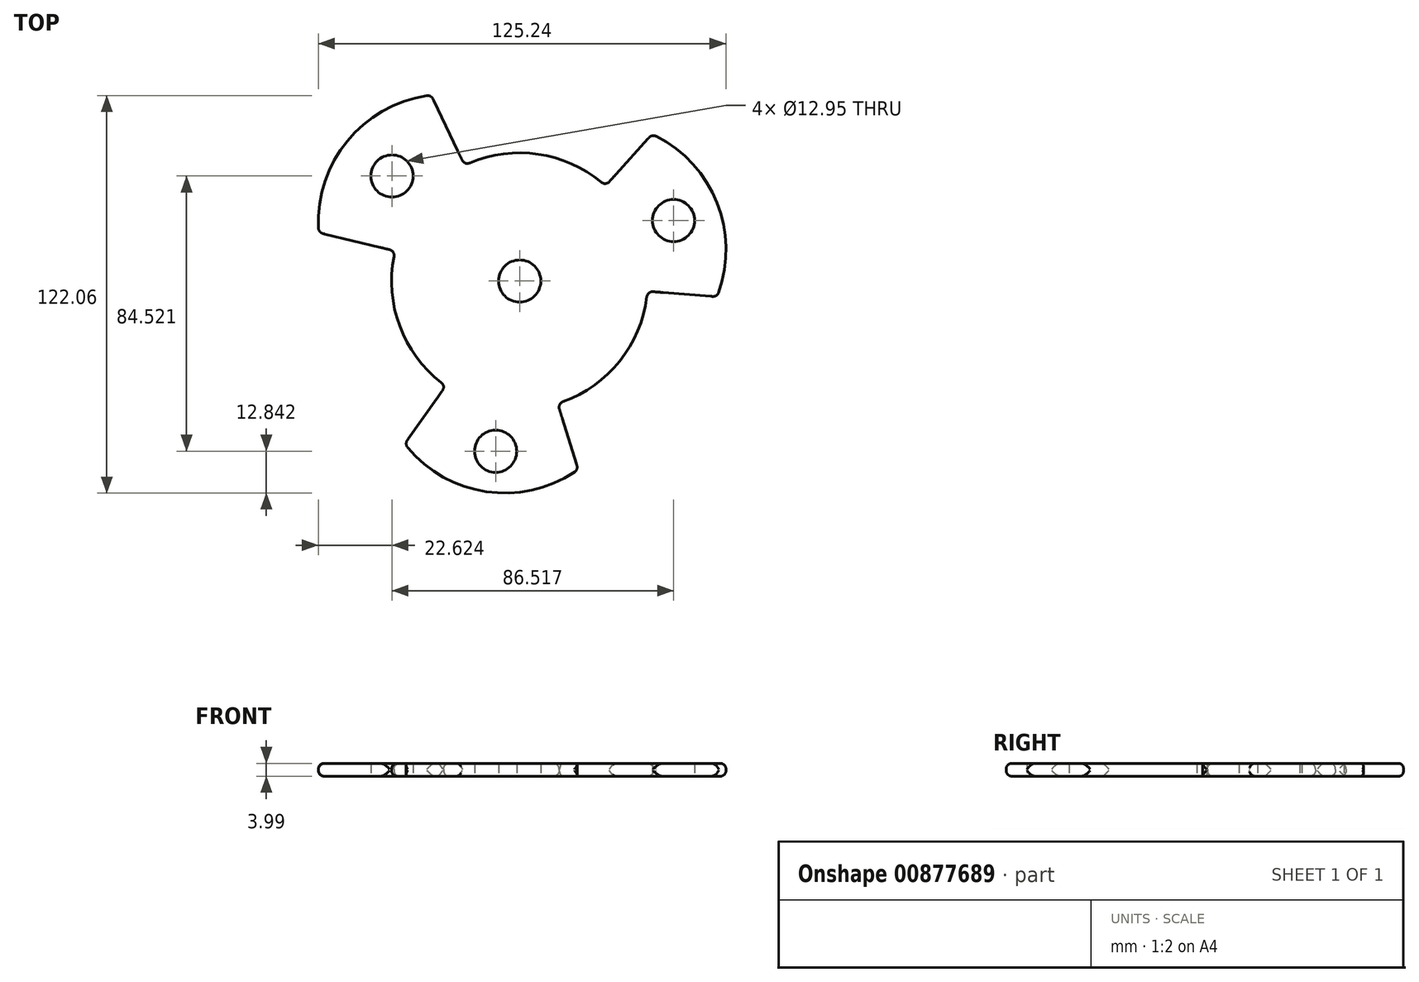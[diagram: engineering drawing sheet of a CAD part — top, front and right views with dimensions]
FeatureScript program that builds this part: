
annotation { "Feature Type Name" : "Feature", "Feature Type Description" : "" }
export const myFeature = defineFeature(function(context is Context, id is Id, definition is map)
    precondition{}
    {
        {
            var Q0;
            Q0=qCreatedBy(makeId("Top.planeOp"),FACE);
            var sketch = newSketch(context, id + "F0", { "sketchPlane" : qUnion([Q0])});
            skCircle(sketch, "E0", {"center": v(-46.46, 55.46) * mm, "radius": 6.48 * mm});
            skCircle(sketch, "E1", {"center": v(40.06, 41.79) * mm, "radius": 6.48 * mm});
            skCircle(sketch, "E2", {"center": v(-14.6, -29.06) * mm, "radius": 6.48 * mm});
            skCircle(sketch, "E3", {"center": v(-7.22, 23.2) * mm, "radius": 6.48 * mm});
            skCircle(sketch, "E4", {"center": v(-7.22, 23.2) * mm, "radius": 39.37 * mm});
            skCircle(sketch, "E5", {"center": v(-7.22, 23.2) * mm, "radius": 35.56 * mm});
            skLineSegment(sketch, "E6", {"start": v(-7.22, 23.2) * mm, "end": v(-68.95, 38.1) * mm});
            skLineSegment(sketch, "E7", {"start": v(-68.95, 38.1) * mm, "end": v(-7.22, 23.2) * mm});
            skLineSegment(sketch, "E8", {"start": v(-7.22, 23.2) * mm, "end": v(-42.53, -26.81) * mm});
            skLineSegment(sketch, "E9", {"start": v(-42.53, -26.81) * mm, "end": v(-7.22, 23.2) * mm});
            skLineSegment(sketch, "E10", {"start": v(-7.22, 23.2) * mm, "end": v(-34.4, 80.31) * mm});
            skLineSegment(sketch, "E11", {"start": v(-34.4, 80.31) * mm, "end": v(-7.22, 23.2) * mm});
            skLineSegment(sketch, "E12", {"start": v(-7.22, 23.2) * mm, "end": v(33.44, 68.27) * mm});
            skLineSegment(sketch, "E13", {"start": v(33.44, 68.27) * mm, "end": v(-7.22, 23.2) * mm});
            skLineSegment(sketch, "E14", {"start": v(53.4, 18.36) * mm, "end": v(-7.22, 23.2) * mm});
            skLineSegment(sketch, "E15", {"start": v(-7.22, 23.2) * mm, "end": v(10.74, -34.68) * mm});
            skArc(sketch, "E16", {"start": v(-34.4, 80.31) * mm, "mid": v(-60.2, 66.18) * mm, "end": v(-68.95, 38.1) * mm});
            skArc(sketch, "E17", {"start": v(53.4, 18.36) * mm, "mid": v(53.37, 47.3) * mm, "end": v(33.44, 68.27) * mm});
            skArc(sketch, "E18", {"start": v(-42.53, -26.81) * mm, "mid": v(-17.48, -41.48) * mm, "end": v(10.74, -34.68) * mm});
            skCircle(sketch, "E19", {"center": v(-7.22, 23.2) * mm, "radius": 10.29 * mm});
            skSolve(sketch);
        }
        {
            var Q0;
            Q0=makeQuery(id+"F0.imprint","IMPRINT",FACE,{"disambiguationData":[TD([[makeQuery(id+"F0.imprint","IMPRINT",EDGE,{"derivedFrom":sQuery(id+"F0.wireOp",EDGE,"E0")}),-1.0]])]});
            var Q1;
            Q1=makeQuery(id+"F0.imprint","IMPRINT",FACE,{"disambiguationData":[TD([[makeQuery(id+"F0.imprint","IMPRINT",EDGE,{"derivedFrom":sQuery(id+"F0.wireOp",EDGE,"E1")}),-1.0]])]});
            var Q2;
            {var subQ0=sQuery(id+"F0.wireOp",EDGE,"8ohev3Rv-3GOB-ZASb-w4sd-z8qtcNEx6lLg");Q2=makeQuery(id+"F0.imprint","IMPRINT",FACE,{"disambiguationData":[TD([[makeQuery(id+"F0.imprint","IMPRINT",EDGE,{"derivedFrom":subQ0}),-1.0]])]});}
            var Q3;
            Q3=makeQuery(id+"F0.imprint","IMPRINT",FACE,{"disambiguationData":[TD([[makeQuery(id+"F0.imprint","IMPRINT",EDGE,{"derivedFrom":sQuery(id+"F0.wireOp",EDGE,"E2")}),-1.0]])]});
            var Q4;
            {var subQ3=sQuery(id+"F0.wireOp",EDGE,"E5");var subQ8=sQuery(id+"F0.wireOp",EDGE,"XuWi3gFe-sEDg-54Sm-Dy0W-UNh7mk1WXWzD");var subQ9=makeQuery(id+"F0.imprint","INTERSECT",VERTEX,{"disambiguationData":[OD(0.0)],"derivedFrom":[subQ8,subQ3]});Q4=makeQuery(id+"F0.imprint","IMPRINT",FACE,{"disambiguationData":[TD([[makeQuery(id+"F0.imprint","IMPRINT",EDGE,{"disambiguationData":[TD([[subQ9,-1.0]])],"derivedFrom":subQ8}),-1.0]])]});}
            var Q5;
            {var subQ4=sQuery(id+"F0.wireOp",EDGE,"XuWi3gFe-sEDg-54Sm-Dy0W-UNh7mk1WXWzD");var subQ5=makeQuery(id+"F0.imprint","INTERSECT",VERTEX,{"derivedFrom":[subQ4,sQuery(id+"F0.wireOp",EDGE,"8ohev3Rv-3GOB-ZASb-w4sd-z8qtcNEx6lLg")]});Q5=makeQuery(id+"F0.imprint","IMPRINT",FACE,{"disambiguationData":[TD([[makeQuery(id+"F0.imprint","IMPRINT",EDGE,{"disambiguationData":[TD([[subQ5,-1.0]])],"derivedFrom":subQ4}),1.0]])]});}
            var Q6;
            {var subQ0=sQuery(id+"F0.wireOp",EDGE,"E5");var subQ1=sQuery(id+"F0.wireOp",EDGE,"XVZgqdlJ-TlGL-cH2d-6rBH-HylyLXSa7ylF");var subQ2=makeQuery(id+"F0.imprint","INTERSECT",VERTEX,{"disambiguationData":[OD(0.0)],"derivedFrom":[subQ1,subQ0]});Q6=makeQuery(id+"F0.imprint","IMPRINT",FACE,{"disambiguationData":[TD([[makeQuery(id+"F0.imprint","IMPRINT",EDGE,{"disambiguationData":[TD([[subQ2,1.0]])],"derivedFrom":subQ1}),1.0]])]});}
            var Q7;
            {var subQ0=sQuery(id+"F0.wireOp",EDGE,"E5");var subQ1=sQuery(id+"F0.wireOp",EDGE,"XuWi3gFe-sEDg-54Sm-Dy0W-UNh7mk1WXWzD");var subQ2=makeQuery(id+"F0.imprint","INTERSECT",VERTEX,{"disambiguationData":[OD(0.0)],"derivedFrom":[subQ1,subQ0]});Q7=makeQuery(id+"F0.imprint","IMPRINT",FACE,{"disambiguationData":[TD([[makeQuery(id+"F0.imprint","IMPRINT",EDGE,{"disambiguationData":[TD([[subQ2,-1.0]])],"derivedFrom":subQ1}),1.0]])]});}
            var Q8;
            {var subQ0=sQuery(id+"F0.wireOp",EDGE,"E5");var subQ1=sQuery(id+"F0.wireOp",EDGE,"xA89MSjh-MWCU-fqti-zXid-59WwbqnXP8Wr");var subQ2=makeQuery(id+"F0.imprint","INTERSECT",VERTEX,{"disambiguationData":[OD(0.0)],"derivedFrom":[subQ1,subQ0]});Q8=makeQuery(id+"F0.imprint","IMPRINT",FACE,{"disambiguationData":[TD([[makeQuery(id+"F0.imprint","IMPRINT",EDGE,{"disambiguationData":[TD([[subQ2,-1.0]])],"derivedFrom":subQ1}),1.0]])]});}
            var Q9;
            {var subQ0=sQuery(id+"F0.wireOp",EDGE,"E11");var subQ1=sQuery(id+"F0.wireOp",EDGE,"E4");var subQ2=makeQuery(id+"F0.imprint","INTERSECT",VERTEX,{"derivedFrom":[subQ1,subQ0]});Q9=makeQuery(id+"F0.imprint","IMPRINT",FACE,{"disambiguationData":[TD([[makeQuery(id+"F0.imprint","IMPRINT",EDGE,{"disambiguationData":[TD([[subQ2,1.0]])],"derivedFrom":subQ1}),1.0]])]});}
            var Q10;
            {var subQ0=sQuery(id+"F0.wireOp",EDGE,"E13");var subQ1=sQuery(id+"F0.wireOp",EDGE,"E4");var subQ2=makeQuery(id+"F0.imprint","INTERSECT",VERTEX,{"derivedFrom":[subQ1,subQ0]});Q10=makeQuery(id+"F0.imprint","IMPRINT",FACE,{"disambiguationData":[TD([[makeQuery(id+"F0.imprint","IMPRINT",EDGE,{"disambiguationData":[TD([[subQ2,1.0]])],"derivedFrom":subQ1}),1.0]])]});}
            var Q11;
            {var subQ0=sQuery(id+"F0.wireOp",EDGE,"E15");var subQ1=sQuery(id+"F0.wireOp",EDGE,"E4");var subQ2=makeQuery(id+"F0.imprint","INTERSECT",VERTEX,{"derivedFrom":[subQ1,subQ0]});Q11=makeQuery(id+"F0.imprint","IMPRINT",FACE,{"disambiguationData":[TD([[makeQuery(id+"F0.imprint","IMPRINT",EDGE,{"disambiguationData":[TD([[subQ2,-1.0]])],"derivedFrom":subQ1}),1.0]])]});}
            var Q12;
            {var subQ0=sQuery(id+"F0.wireOp",EDGE,"E9");var subQ1=sQuery(id+"F0.wireOp",EDGE,"E4");var subQ2=makeQuery(id+"F0.imprint","INTERSECT",VERTEX,{"derivedFrom":[subQ1,subQ0]});Q12=makeQuery(id+"F0.imprint","IMPRINT",FACE,{"disambiguationData":[TD([[makeQuery(id+"F0.imprint","IMPRINT",EDGE,{"disambiguationData":[TD([[subQ2,-1.0]])],"derivedFrom":subQ1}),1.0]])]});}
            var Q13;
            {var subQ0=sQuery(id+"F0.wireOp",EDGE,"E7");var subQ1=sQuery(id+"F0.wireOp",EDGE,"E4");var subQ2=makeQuery(id+"F0.imprint","INTERSECT",VERTEX,{"derivedFrom":[subQ1,subQ0]});Q13=makeQuery(id+"F0.imprint","IMPRINT",FACE,{"disambiguationData":[TD([[makeQuery(id+"F0.imprint","IMPRINT",EDGE,{"disambiguationData":[TD([[subQ2,-1.0]])],"derivedFrom":subQ1}),1.0]])]});}
            var Q14;
            {var subQ0=sQuery(id+"F0.wireOp",EDGE,"E11");var subQ1=sQuery(id+"F0.wireOp",EDGE,"E4");var subQ2=makeQuery(id+"F0.imprint","INTERSECT",VERTEX,{"derivedFrom":[subQ1,subQ0]});Q14=makeQuery(id+"F0.imprint","IMPRINT",FACE,{"disambiguationData":[TD([[makeQuery(id+"F0.imprint","IMPRINT",EDGE,{"disambiguationData":[TD([[subQ2,-1.0]])],"derivedFrom":subQ1}),1.0]])]});}
            var Q15;
            {var subQ0=sQuery(id+"F0.wireOp",EDGE,"E11");var subQ1=sQuery(id+"F0.wireOp",EDGE,"E5");var subQ2=makeQuery(id+"F0.imprint","INTERSECT",VERTEX,{"derivedFrom":[subQ1,subQ0]});Q15=makeQuery(id+"F0.imprint","IMPRINT",FACE,{"disambiguationData":[TD([[makeQuery(id+"F0.imprint","IMPRINT",EDGE,{"disambiguationData":[TD([[subQ2,-1.0]])],"derivedFrom":subQ1}),1.0]])]});}
            var Q16;
            {var subQ0=sQuery(id+"F0.wireOp",EDGE,"E13");var subQ1=sQuery(id+"F0.wireOp",EDGE,"E5");var subQ2=makeQuery(id+"F0.imprint","INTERSECT",VERTEX,{"derivedFrom":[subQ1,subQ0]});Q16=makeQuery(id+"F0.imprint","IMPRINT",FACE,{"disambiguationData":[TD([[makeQuery(id+"F0.imprint","IMPRINT",EDGE,{"disambiguationData":[TD([[subQ2,1.0]])],"derivedFrom":subQ1}),1.0]])]});}
            var Q17;
            {var subQ0=sQuery(id+"F0.wireOp",EDGE,"E9");var subQ1=sQuery(id+"F0.wireOp",EDGE,"E5");var subQ2=makeQuery(id+"F0.imprint","INTERSECT",VERTEX,{"derivedFrom":[subQ1,subQ0]});Q17=makeQuery(id+"F0.imprint","IMPRINT",FACE,{"disambiguationData":[TD([[makeQuery(id+"F0.imprint","IMPRINT",EDGE,{"disambiguationData":[TD([[subQ2,-1.0]])],"derivedFrom":subQ1}),1.0]])]});}
            var Q18;
            {var subQ0=sQuery(id+"F0.wireOp",EDGE,"E9");var subQ1=sQuery(id+"F0.wireOp",EDGE,"E3");var subQ2=makeQuery(id+"F0.imprint","INTERSECT",VERTEX,{"derivedFrom":[subQ1,subQ0]});Q18=makeQuery(id+"F0.imprint","IMPRINT",FACE,{"disambiguationData":[TD([[makeQuery(id+"F0.imprint","IMPRINT",EDGE,{"disambiguationData":[TD([[subQ2,-1.0]])],"derivedFrom":subQ1}),-1.0]])]});}
            var Q19;
            {var subQ0=sQuery(id+"F0.wireOp",EDGE,"E7");var subQ1=sQuery(id+"F0.wireOp",EDGE,"E3");var subQ2=makeQuery(id+"F0.imprint","INTERSECT",VERTEX,{"derivedFrom":[subQ1,subQ0]});Q19=makeQuery(id+"F0.imprint","IMPRINT",FACE,{"disambiguationData":[TD([[makeQuery(id+"F0.imprint","IMPRINT",EDGE,{"disambiguationData":[TD([[subQ2,-1.0]])],"derivedFrom":subQ1}),-1.0]])]});}
            var Q20;
            {var subQ0=sQuery(id+"F0.wireOp",EDGE,"E11");var subQ1=sQuery(id+"F0.wireOp",EDGE,"E3");var subQ2=makeQuery(id+"F0.imprint","INTERSECT",VERTEX,{"derivedFrom":[subQ1,subQ0]});Q20=makeQuery(id+"F0.imprint","IMPRINT",FACE,{"disambiguationData":[TD([[makeQuery(id+"F0.imprint","IMPRINT",EDGE,{"disambiguationData":[TD([[subQ2,-1.0]])],"derivedFrom":subQ1}),-1.0]])]});}
            var Q21;
            {var subQ0=sQuery(id+"F0.wireOp",EDGE,"E11");var subQ1=sQuery(id+"F0.wireOp",EDGE,"E3");var subQ2=makeQuery(id+"F0.imprint","INTERSECT",VERTEX,{"derivedFrom":[subQ1,subQ0]});Q21=makeQuery(id+"F0.imprint","IMPRINT",FACE,{"disambiguationData":[TD([[makeQuery(id+"F0.imprint","IMPRINT",EDGE,{"disambiguationData":[TD([[subQ2,1.0]])],"derivedFrom":subQ1}),-1.0]])]});}
            var Q22;
            {var subQ0=sQuery(id+"F0.wireOp",EDGE,"E13");var subQ1=sQuery(id+"F0.wireOp",EDGE,"E3");var subQ2=makeQuery(id+"F0.imprint","INTERSECT",VERTEX,{"derivedFrom":[subQ1,subQ0]});Q22=makeQuery(id+"F0.imprint","IMPRINT",FACE,{"disambiguationData":[TD([[makeQuery(id+"F0.imprint","IMPRINT",EDGE,{"disambiguationData":[TD([[subQ2,1.0]])],"derivedFrom":subQ1}),-1.0]])]});}
            var Q23;
            {var subQ0=sQuery(id+"F0.wireOp",EDGE,"E15");var subQ1=sQuery(id+"F0.wireOp",EDGE,"E3");var subQ2=makeQuery(id+"F0.imprint","INTERSECT",VERTEX,{"derivedFrom":[subQ1,subQ0]});Q23=makeQuery(id+"F0.imprint","IMPRINT",FACE,{"disambiguationData":[TD([[makeQuery(id+"F0.imprint","IMPRINT",EDGE,{"disambiguationData":[TD([[subQ2,-1.0]])],"derivedFrom":subQ1}),-1.0]])]});}
            extrude(context, id + "F1", {"entities" : qUnion([Q0, Q1, Q2, Q3, Q4, Q5, Q6, Q7, Q8, Q9, Q10, Q11, Q12, Q13, Q14, Q15, Q16, Q17, Q18, Q19, Q20, Q21, Q22, Q23]), "depth" : 4 * mm, "offsetDistance" : 25.4 * mm});
        }
        {
            var Q0;
            Q0=makeQuery(id+"F1.opExtrude","SWEPT_FACE",FACE,{"disambiguationData":[OSD([sQuery(id+"F0.wireOp",EDGE,"E4")])]});
            var Q1;
            Q1=makeQuery(id+"F1.opExtrude","CAP_EDGE",EDGE,{"disambiguationData":[OSD([sQuery(id+"F0.wireOp",EDGE,"E4")])],"isStart":true});
            var Q2;
            {var subQ0=sQuery(id+"F0.wireOp",EDGE,"E5");Q2=makeQuery(id+"F1.opExtrude","SWEPT_FACE",FACE,{"disambiguationData":[OSD([subQ0]),TDD([makeQuery(id+"F0.imprint","IMPRINT",EDGE,{"disambiguationData":[TD([[makeQuery(id+"F0.imprint","INTERSECT",VERTEX,{"disambiguationData":[OD(0.0)],"derivedFrom":[sQuery(id+"F0.wireOp",EDGE,"XuWi3gFe-sEDg-54Sm-Dy0W-UNh7mk1WXWzD"),subQ0]}),1.0]])],"derivedFrom":subQ0})])]});}
            var Q3;
            {var subQ0=sQuery(id+"F0.wireOp",EDGE,"E5");Q3=makeQuery(id+"F1.opExtrude","SWEPT_FACE",FACE,{"disambiguationData":[OSD([subQ0]),TDD([makeQuery(id+"F0.imprint","IMPRINT",EDGE,{"disambiguationData":[TD([[makeQuery(id+"F0.imprint","INTERSECT",VERTEX,{"disambiguationData":[OD(1.0)],"derivedFrom":[sQuery(id+"F0.wireOp",EDGE,"XuWi3gFe-sEDg-54Sm-Dy0W-UNh7mk1WXWzD"),subQ0]}),-1.0]])],"derivedFrom":subQ0})])]});}
            var Q4;
            {var subQ0=sQuery(id+"F0.wireOp",EDGE,"E5");Q4=makeQuery(id+"F1.opExtrude","SWEPT_FACE",FACE,{"disambiguationData":[OSD([subQ0]),TDD([makeQuery(id+"F0.imprint","IMPRINT",EDGE,{"disambiguationData":[TD([[makeQuery(id+"F0.imprint","INTERSECT",VERTEX,{"disambiguationData":[OD(0.0)],"derivedFrom":[sQuery(id+"F0.wireOp",EDGE,"XVZgqdlJ-TlGL-cH2d-6rBH-HylyLXSa7ylF"),subQ0]}),-1.0]])],"derivedFrom":subQ0})])]});}
            var Q5;
            Q5=makeQuery(id+"F1.opExtrude","SWEPT_FACE",FACE,{"disambiguationData":[OSD([sQuery(id+"F0.wireOp",EDGE,"E17")])]});
            var Q6;
            Q6=makeQuery(id+"F1.opExtrude","SWEPT_FACE",FACE,{"disambiguationData":[OSD([sQuery(id+"F0.wireOp",EDGE,"E16")])]});
            var Q7;
            Q7=makeQuery(id+"F1.opExtrude","SWEPT_FACE",FACE,{"disambiguationData":[OSD([sQuery(id+"F0.wireOp",EDGE,"E18")])]});
            fillet(context, id + "F2", {"entities" : qUnion([Q0, Q1, Q2, Q3, Q4, Q5, Q6, Q7]), "radius" : 1.78 * mm, "tangentPropagation" : true, "allowEdgeOverflow" : false});
        }
    });
